annotation { "Feature Type Name" : "Feature", "Feature Type Description" : "" }
export const myFeature = defineFeature(function(context is Context, id is Id, definition is map)
    precondition{}
    {
        {
            var Q0;
            Q0=qCreatedBy(makeId("Front.planeOp"),FACE);
            var sketch = newSketch(context, id + "F0", { "sketchPlane" : qUnion([Q0])});
            skCircle(sketch, "E0", {"center": v(5.32, 6.15) * mm, "radius": 3.81 * mm});
            skCircle(sketch, "E1", {"center": v(34.53, 6.15) * mm, "radius": 3.81 * mm});
            skCircle(sketch, "E2", {"center": v(5.32, 49.42) * mm, "radius": 3.81 * mm});
            skCircle(sketch, "E3", {"center": v(34.53, 49.42) * mm, "radius": 3.81 * mm});
            skCircle(sketch, "E4", {"center": v(65.34, 41.87) * mm, "radius": 3.81 * mm});
            skCircle(sketch, "E5", {"center": v(65.34, 12.66) * mm, "radius": 3.81 * mm});
            skArc(sketch, "E6", {"start": v(38.21, 50.38) * mm, "mid": v(48.9, 40.65) * mm, "end": v(62.77, 44.68) * mm});
            skArc(sketch, "E7", {"start": v(32.3, 46.33) * mm, "mid": v(46.6, 36.4) * mm, "end": v(63.89, 38.35) * mm});
            skArc(sketch, "E8", {"start": v(35.47, 2.46) * mm, "mid": v(53.6, -5.84) * mm, "end": v(66.78, 9.14) * mm});
            skArc(sketch, "E9", {"start": v(38.21, 5.18) * mm, "mid": v(52.45, -2.8) * mm, "end": v(62.81, 9.81) * mm});
            skFitSpline(sketch, "E10", {"points": [v(2.04, 8.1) * mm, v(-10.8, 15.37) * mm, v(-6.63, 25.02) * mm, v(2.65, 32.03) * mm, v(8.14, 39.22) * mm, v(3.23, 46.23) * mm], "startDerivative": vector(-74.98, 24.62) * mm, "endDerivative": vector(-41.71, 38.58) * mm});
            skFitSpline(sketch, "E11", {"points": [v(9.03, 48.54) * mm, v(13.63, 40.55) * mm, v(7.76, 29.57) * mm, v(-2.28, 22.37) * mm, v(-5.12, 16.12) * mm, v(6.55, 9.76) * mm], "startDerivative": vector(36.04, -39.7) * mm, "endDerivative": vector(71.6, -24.47) * mm});
            skText(sketch, "E12", { "text": "Circuit Scribe", "fontName": "OpenSans-Regular.ttf"});
            const initialGuessF0  = {"E12": [0.01552, -0.01464, 1, 0, 0.00598]};
            skSetInitialGuess(sketch, initialGuessF0);
            skSolve(sketch);
        }
        {
            var Q0;
            Q0 = qSketchRegion(id + "F0", true);
            extrude(context, id + "F1", {"entities" : qUnion([Q0]), "depth" : 5.08 * mm, "offsetDistance" : 25.4 * mm});
        }
    });